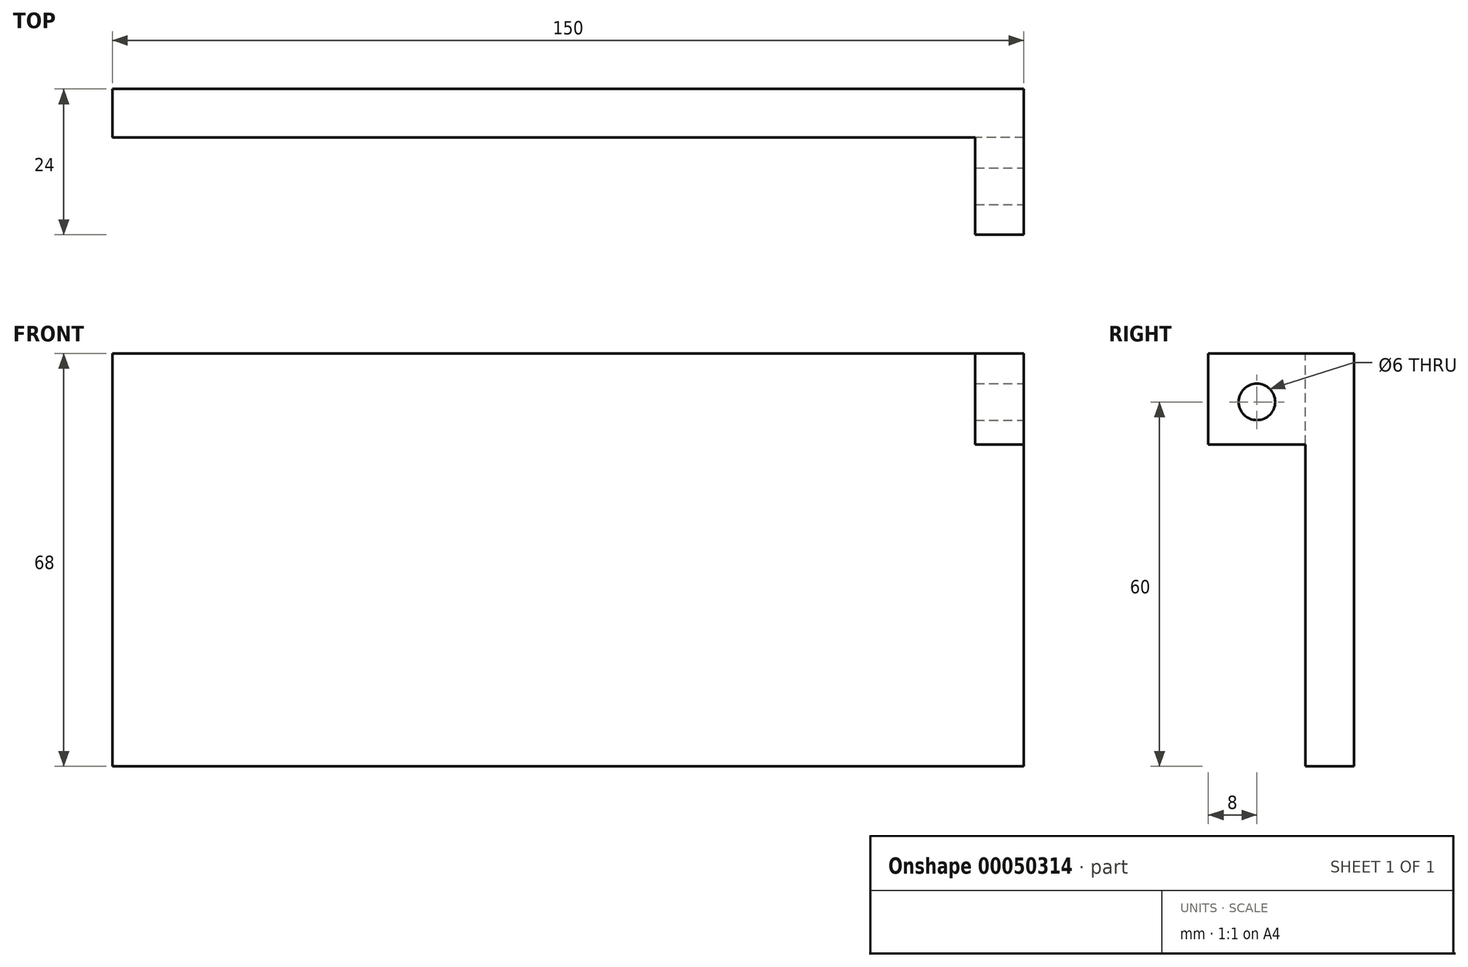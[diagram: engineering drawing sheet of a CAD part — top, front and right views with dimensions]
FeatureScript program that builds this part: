
annotation { "Feature Type Name" : "Feature", "Feature Type Description" : "" }
export const myFeature = defineFeature(function(context is Context, id is Id, definition is map)
    precondition{}
    {
        {
            var Q0;
            Q0=qCreatedBy(makeId("Front.planeOp"),FACE);
            var sketch = newSketch(context, id + "F0", { "sketchPlane" : qUnion([Q0])});
            skLineSegment(sketch, "E0.bottom", {"start": v(0, 0) * mm, "end": v(-150, 0) * mm});
            skLineSegment(sketch, "E0.top", {"start": v(0, -68) * mm, "end": v(-150, -68) * mm});
            skLineSegment(sketch, "E0.left", {"start": v(0, 0) * mm, "end": v(0, -68) * mm});
            skLineSegment(sketch, "E0.right", {"start": v(-150, 0) * mm, "end": v(-150, -68) * mm});
            skSolve(sketch);
        }
        {
            var Q0;
            Q0 = qSketchRegion(id + "F0", true);
            extrude(context, id + "F1", {"entities" : qUnion([Q0]), "depth" : 8 * mm});
        }
        {
            var Q0;
            Q0=makeQuery(id+"F1.opExtrude","SWEPT_FACE",FACE,{"disambiguationData":[OSD([sQuery(id+"F0.wireOp",EDGE,"E0.left")])]});
            var sketch = newSketch(context, id + "F2", { "sketchPlane" : qUnion([Q0])});
            skLineSegment(sketch, "E1.bottom", {"start": v(0, 0) * mm, "end": v(-24, 0) * mm});
            skLineSegment(sketch, "E1.top", {"start": v(0, -15) * mm, "end": v(-24, -15) * mm});
            skLineSegment(sketch, "E1.left", {"start": v(0, 0) * mm, "end": v(0, -15) * mm});
            skLineSegment(sketch, "E1.right", {"start": v(-24, 0) * mm, "end": v(-24, -15) * mm});
            skCircle(sketch, "E2", {"center": v(-16, -8) * mm, "radius": 3 * mm});
            skSolve(sketch);
        }
        {
            var Q0;
            Q0 = qSketchRegion(id + "F2", true);
            extrude(context, id + "F3", {"entities" : qUnion([Q0]), "operationType" : NewBodyOperationType.ADD, "oppositeDirection" : true, "depth" : 8 * mm});
        }
    });
